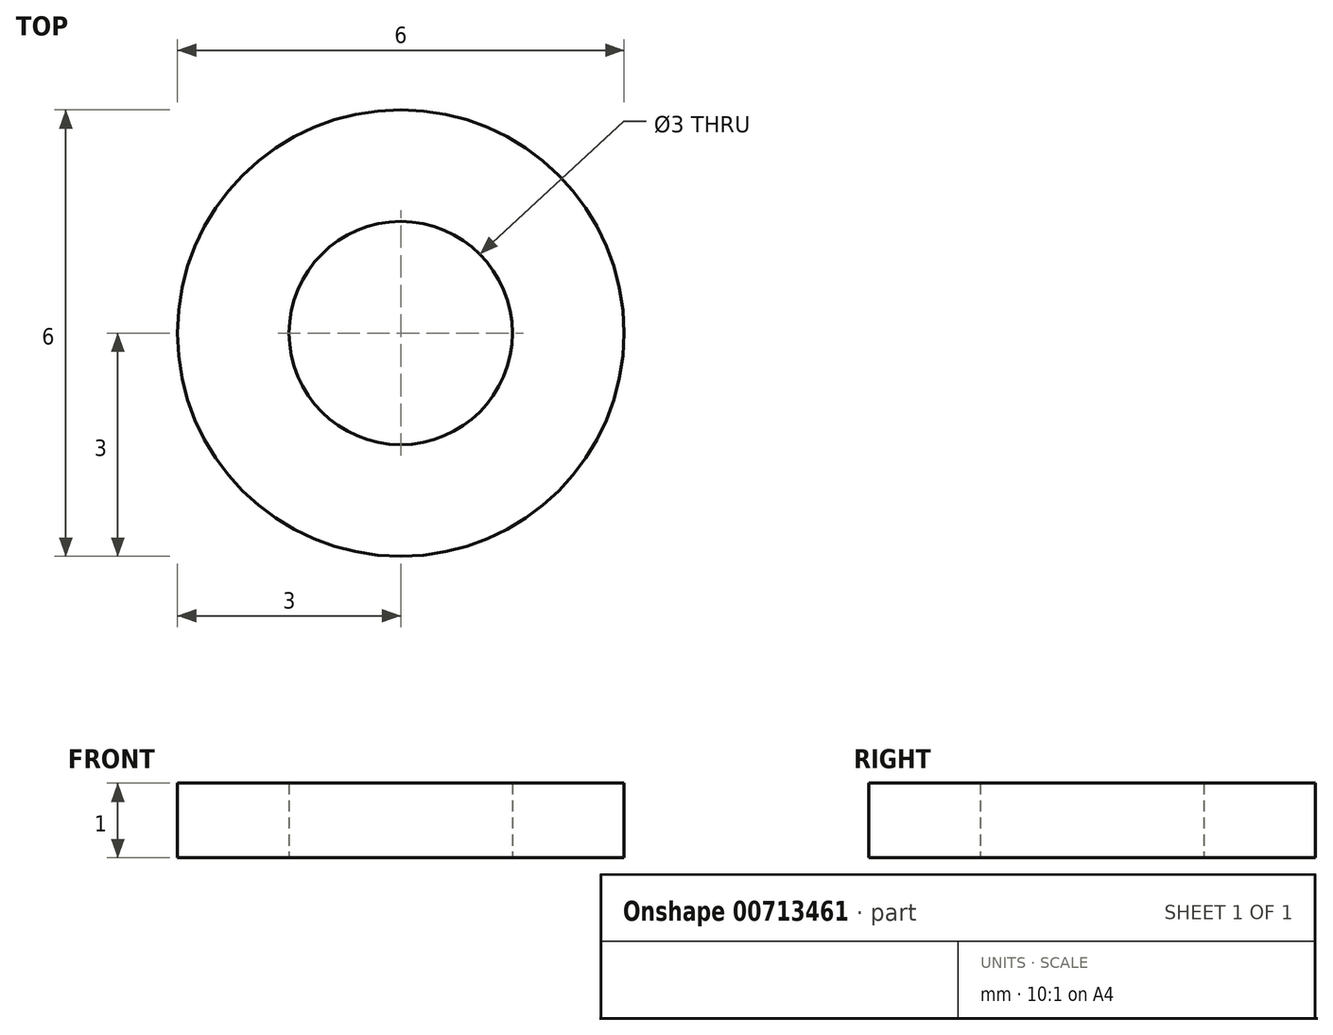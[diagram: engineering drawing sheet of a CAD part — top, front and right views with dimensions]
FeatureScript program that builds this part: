
annotation { "Feature Type Name" : "Feature", "Feature Type Description" : "" }
export const myFeature = defineFeature(function(context is Context, id is Id, definition is map)
    precondition{}
    {
        {
            var Q0;
            Q0=qCreatedBy(makeId("Top.planeOp"),FACE);
            var sketch = newSketch(context, id + "F0", { "sketchPlane" : qUnion([Q0])});
            skCircle(sketch, "E0", {"center": v(0, 0) * mm, "radius": 1.5 * mm});
            skCircle(sketch, "E1", {"center": v(0, 0) * mm, "radius": 3 * mm});
            skSolve(sketch);
        }
        {
            var Q0;
            Q0 = qSketchRegion(id + "F0", true);
            extrude(context, id + "F1", {"entities" : qUnion([Q0]), "depth" : 1 * mm, "offsetDistance" : 25 * mm});
        }
    });
